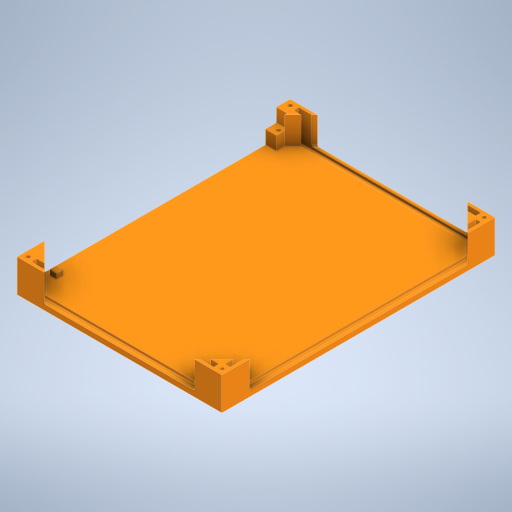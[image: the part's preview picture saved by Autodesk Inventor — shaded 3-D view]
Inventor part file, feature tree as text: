
AUTODESK INVENTOR PART (.ipt)
format: ipt  version: 2024.3 (Build 283343000, 343)  size: 410,624 bytes
history: native  units: mm
features: sketch x9, extrude x7, other x3, mirror x3, hole x2, pattern_circular x1, fillet x1
ambient origin geometry x8: Origin, YZ Plane, XZ Plane, XY Plane, X Axis, Y Axis, Z Axis, Center Point
bodies: Body1 (feature_tree)
feature tree (26):
  other  "Těleso1"
  extrude  "Vysunutí1"  Depth=200.0mm
  extrude  "Vysunutí7"  Depth=150.0mm
  mirror  "Zrcadlit5"
  other  "Pracovní rovina2"
  hole  "Díra4"  [1 undecoded]
  pattern_circular  "Kruhové pole1"  Count=2  [1 undecoded]
  mirror  "Zrcadlit6"
  extrude  "Vysunutí9"  Depth=4.0mm
  mirror  "Zrcadlit7"
  extrude  "Vysunutí10"  Depth=2.0mm
  extrude  "Vysunutí11"  Depth=8.0mm
  fillet  "Zaoblení1"  Radius=10.0mm
  extrude  "Vysunutí12"  Depth=6.0mm
  sketch  "Náčrt16"
  other  "Pracovní rovina3"
  extrude  "Vysunutí14"  Depth=20.0mm
  hole  "Díra6"  [1 undecoded]
  sketch  "Náčrt1"
  sketch  "Náčrt2"
  sketch  "Náčrt11"
  sketch  "Náčrt12"
  sketch  "Náčrt13"
  sketch  "Náčrt14"
  sketch  "Náčrt15"
  sketch  "Náčrt18"
note: 3 required parameter values undecoded (feature->parameter linkage not recoverable at this tier; creation-order binding heuristic only, values carry confidence <= 0.55)
